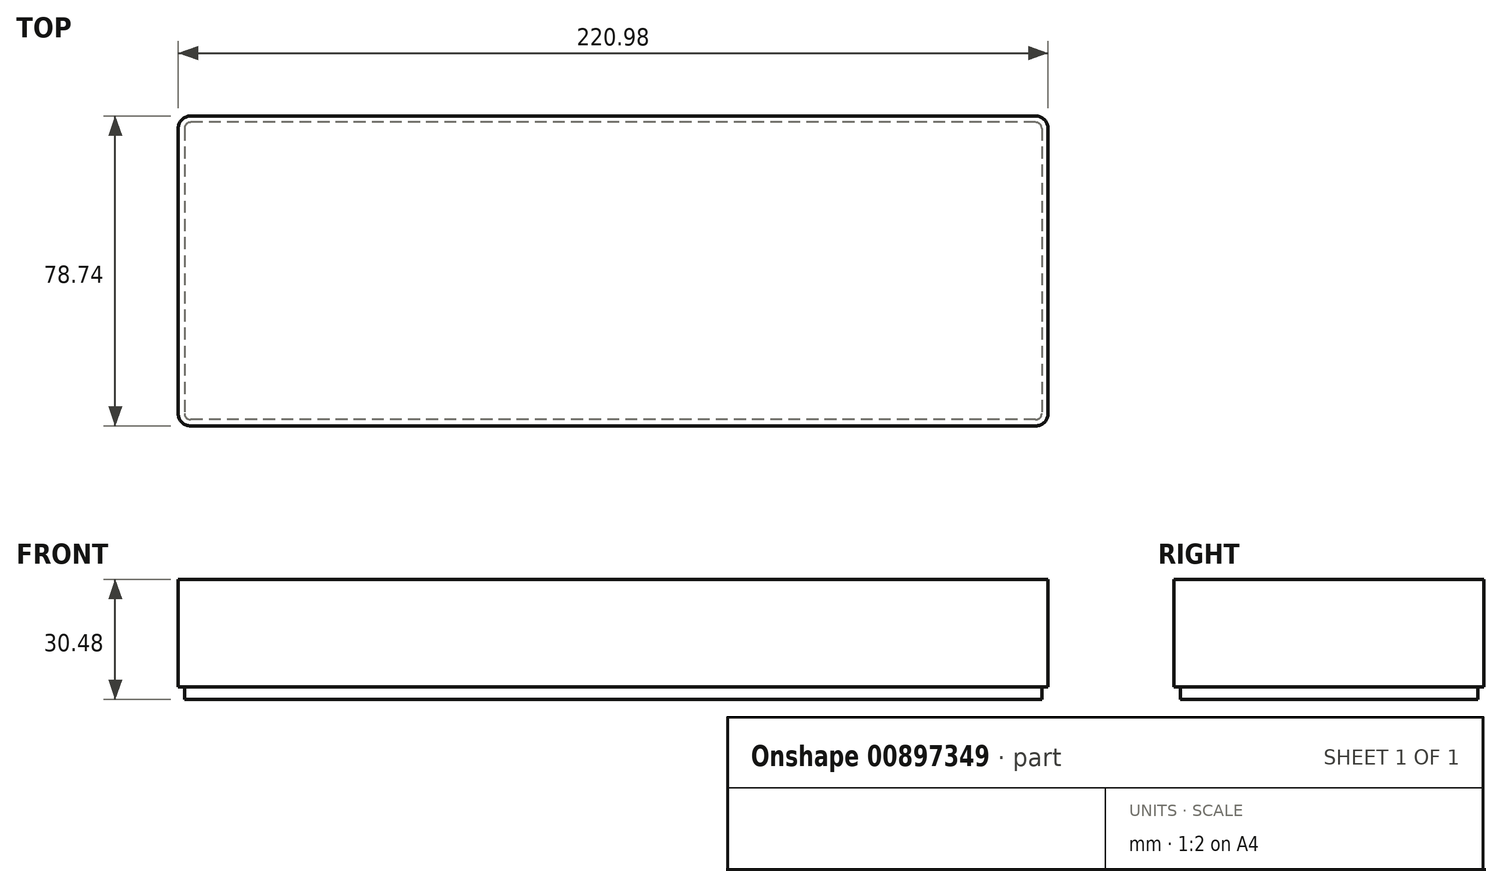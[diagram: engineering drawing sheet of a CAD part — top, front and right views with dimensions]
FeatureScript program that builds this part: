
annotation { "Feature Type Name" : "Feature", "Feature Type Description" : "" }
export const myFeature = defineFeature(function(context is Context, id is Id, definition is map)
    precondition{}
    {
        {
            var Q0;
            Q0=qCreatedBy(makeId("Top.planeOp"),FACE);
            var sketch = newSketch(context, id + "F0", { "sketchPlane" : qUnion([Q0])});
            skLineSegment(sketch, "E0.bottom", {"start": v(110.5, 39.37) * mm, "end": v(-110.5, 39.37) * mm});
            skLineSegment(sketch, "E0.top", {"start": v(110.5, -39.37) * mm, "end": v(-110.5, -39.37) * mm});
            skLineSegment(sketch, "E0.left", {"start": v(110.5, 39.37) * mm, "end": v(110.5, -39.37) * mm});
            skLineSegment(sketch, "E0.right", {"start": v(-110.5, 39.37) * mm, "end": v(-110.5, -39.37) * mm});
            skPoint(sketch, "E0.middle", {"position": v(0, 0) * mm});
            skSolve(sketch);
        }
        {
            var Q0;
            Q0=makeQuery(id+"F0.imprint","IMPRINT",FACE,{"disambiguationData":[TD([[makeQuery(id+"F0.imprint","IMPRINT",EDGE,{"derivedFrom":sQuery(id+"F0.wireOp",EDGE,"E0.bottom")}),1.0]])]});
            extrude(context, id + "F1", {"entities" : qUnion([Q0]), "depth" : 30.48 * mm, "offsetDistance" : 25.4 * mm});
        }
        {
            var Q0;
            Q0=makeQuery(id+"F1.opExtrude","SWEPT_EDGE",EDGE,{"disambiguationData":[OSD([sQuery(id+"F0.wireOp",EDGE,"E0.top"),sQuery(id+"F0.wireOp",EDGE,"E0.right")])]});
            var Q1;
            Q1=makeQuery(id+"F1.opExtrude","SWEPT_EDGE",EDGE,{"disambiguationData":[OSD([sQuery(id+"F0.wireOp",EDGE,"E0.bottom"),sQuery(id+"F0.wireOp",EDGE,"E0.left")])]});
            var Q2;
            Q2=makeQuery(id+"F1.opExtrude","SWEPT_EDGE",EDGE,{"disambiguationData":[OSD([sQuery(id+"F0.wireOp",EDGE,"E0.top"),sQuery(id+"F0.wireOp",EDGE,"E0.left")])]});
            var Q3;
            Q3=makeQuery(id+"F1.opExtrude","SWEPT_EDGE",EDGE,{"disambiguationData":[OSD([sQuery(id+"F0.wireOp",EDGE,"E0.bottom"),sQuery(id+"F0.wireOp",EDGE,"E0.right")])]});
            fillet(context, id + "F2", {"entities" : qUnion([Q0, Q1, Q2, Q3]), "radius" : 3.17 * mm, "tangentPropagation" : true, "allowEdgeOverflow" : false});
        }
        {
            var Q0;
            Q0=makeQuery(id+"F1.opExtrude","CAP_FACE",FACE,{"disambiguationData":[OSD([sQuery(id+"F0.wireOp",EDGE,"E0.bottom"),sQuery(id+"F0.wireOp",EDGE,"E0.top"),sQuery(id+"F0.wireOp",EDGE,"E0.left"),sQuery(id+"F0.wireOp",EDGE,"E0.right")])],"isStart":true});
            var sketch = newSketch(context, id + "F3", { "sketchPlane" : qUnion([Q0])});
            skLineSegment(sketch, "E1.0", {"start": v(107.32, 39.37) * mm, "end": v(-107.32, 39.37) * mm});
            skLineSegment(sketch, "E2.0", {"start": v(-110.5, -36.2) * mm, "end": v(-110.5, 36.2) * mm});
            skArc(sketch, "E3.0", {"start": v(-107.32, 39.37) * mm, "mid": v(-109.56, 38.44) * mm, "end": v(-110.5, 36.2) * mm});
            skArc(sketch, "E4.0", {"start": v(-110.5, -36.2) * mm, "mid": v(-109.56, -38.44) * mm, "end": v(-107.32, -39.37) * mm});
            skLineSegment(sketch, "E5.0", {"start": v(107.32, -39.37) * mm, "end": v(-107.32, -39.37) * mm});
            skLineSegment(sketch, "E6.0", {"start": v(110.5, -36.2) * mm, "end": v(110.5, 36.2) * mm});
            skArc(sketch, "E7.0", {"start": v(107.32, -39.37) * mm, "mid": v(109.56, -38.44) * mm, "end": v(110.5, -36.2) * mm});
            skArc(sketch, "E8.0", {"start": v(110.5, 36.2) * mm, "mid": v(109.56, 38.44) * mm, "end": v(107.32, 39.37) * mm});
            skArc(sketch, "E9.0", {"start": v(108.9, 36.2) * mm, "mid": v(108.44, 37.32) * mm, "end": v(107.32, 37.78) * mm});
            skLineSegment(sketch, "E9.1", {"start": v(108.9, -36.2) * mm, "end": v(108.9, 36.2) * mm});
            skLineSegment(sketch, "E9.2", {"start": v(107.32, 37.78) * mm, "end": v(-107.32, 37.78) * mm});
            skArc(sketch, "E9.3", {"start": v(107.32, -37.78) * mm, "mid": v(108.44, -37.32) * mm, "end": v(108.9, -36.2) * mm});
            skArc(sketch, "E9.4", {"start": v(-107.32, 37.78) * mm, "mid": v(-108.44, 37.32) * mm, "end": v(-108.9, 36.2) * mm});
            skLineSegment(sketch, "E9.5", {"start": v(-108.9, -36.2) * mm, "end": v(-108.9, 36.2) * mm});
            skArc(sketch, "E9.6", {"start": v(-108.9, -36.2) * mm, "mid": v(-108.44, -37.32) * mm, "end": v(-107.32, -37.78) * mm});
            skLineSegment(sketch, "E9.7", {"start": v(107.32, -37.78) * mm, "end": v(-107.32, -37.78) * mm});
            skSolve(sketch);
        }
        {
            var Q0;
            Q0=makeQuery(id+"F3.imprint","IMPRINT",FACE,{"disambiguationData":[TD([[makeQuery(id+"F3.imprint","IMPRINT",EDGE,{"derivedFrom":sQuery(id+"F3.wireOp",EDGE,"E1.0")}),1.0]])]});
            extrude(context, id + "F4", {"entities" : qUnion([Q0]), "operationType" : NewBodyOperationType.REMOVE, "oppositeDirection" : true, "depth" : 3.17 * mm, "offsetDistance" : 25.4 * mm});
        }
    });
